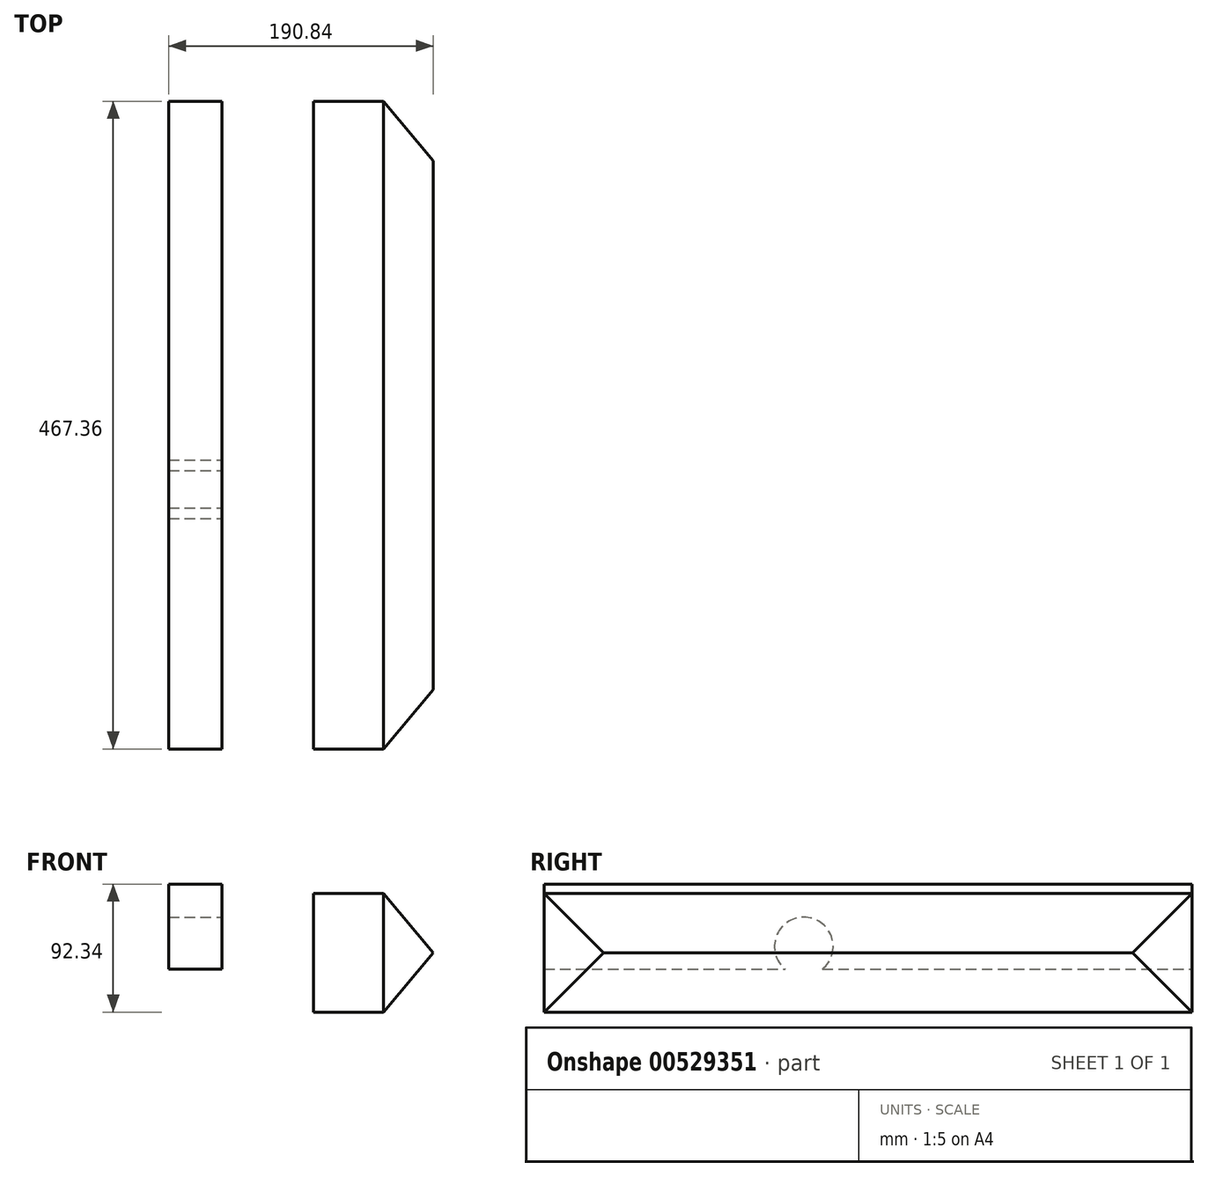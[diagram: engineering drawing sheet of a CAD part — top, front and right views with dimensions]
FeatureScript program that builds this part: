
annotation { "Feature Type Name" : "Feature", "Feature Type Description" : "" }
export const myFeature = defineFeature(function(context is Context, id is Id, definition is map)
    precondition{}
    {
        {
            var Q0;
            Q0=qCreatedBy(makeId("Front.planeOp"),FACE);
            var sketch = newSketch(context, id + "F0", { "sketchPlane" : qUnion([Q0])});
            skLineSegment(sketch, "E0.bottom", {"start": v(-55.25, 54.7) * mm, "end": v(-16.83, 54.7) * mm});
            skLineSegment(sketch, "E0.top", {"start": v(-55.25, -6.63) * mm, "end": v(-16.83, -6.63) * mm});
            skLineSegment(sketch, "E0.left", {"start": v(-55.25, 54.7) * mm, "end": v(-55.25, -6.63) * mm});
            skLineSegment(sketch, "E0.right", {"start": v(-16.83, 54.7) * mm, "end": v(-16.83, -6.63) * mm});
            skLineSegment(sketch, "E1.bottom", {"start": v(49.3, 48.02) * mm, "end": v(99.65, 48.02) * mm});
            skLineSegment(sketch, "E1.top", {"start": v(49.3, -37.65) * mm, "end": v(99.65, -37.65) * mm});
            skLineSegment(sketch, "E1.left", {"start": v(49.3, 48.02) * mm, "end": v(49.3, -37.65) * mm});
            skLineSegment(sketch, "E1.right", {"start": v(99.65, 48.02) * mm, "end": v(99.65, -37.65) * mm});
            skSolve(sketch);
        }
        {
            var Q0;
            Q0 = qSketchRegion(id + "F0", true);
            extrude(context, id + "F1", {"entities" : qUnion([Q0]), "depth" : 467.36 * mm, "offsetDistance" : 25.4 * mm});
        }
        {
            var Q0;
            Q0=makeQuery(id+"F1.opExtrude","SWEPT_FACE",FACE,{"disambiguationData":[OSD([sQuery(id+"F0.wireOp",EDGE,"E1.right")])]});
            var sketch = newSketch(context, id + "F2", { "sketchPlane" : qUnion([Q0])});
            skPoint(sketch, "E2", {"position": v(-280.03, 9.7) * mm});
            skSolve(sketch);
        }
        {
            var Q0;
            Q0=sQuery(id+"F2.wireOp",VERTEX,"E2");
            var Q1;
            Q1=makeQuery(id+"F1.opExtrude","SWEPT_BODY",BODY,{"disambiguationData":[OSD([sQuery(id+"F0.wireOp",EDGE,"E0.bottom"),sQuery(id+"F0.wireOp",EDGE,"E0.top"),sQuery(id+"F0.wireOp",EDGE,"E0.left"),sQuery(id+"F0.wireOp",EDGE,"E0.right")])]});
            hole(context, id + "F3", {"style" : HoleStyle.SIMPLE, "endStyle" : HoleEndStyle.THROUGH, "holeDiameter" : 42.32 * mm, "isTappedThrough" : true, "tappedDepth" : 12.7 * mm, "tapClearance" : 3, "startFromSketch" : true, "locations" : qUnion([Q0]), "scope" : qUnion([Q1])});
        }
        {
            var Q0;
            Q0=makeQuery(id+"F1.opExtrude","SWEPT_FACE",FACE,{"disambiguationData":[OSD([sQuery(id+"F0.wireOp",EDGE,"E1.right")])]});
            extrude(context, id + "F4", {"entities" : qUnion([Q0]), "operationType" : NewBodyOperationType.ADD, "depth" : 294.64 * mm, "offsetDistance" : 25.4 * mm, "hasDraft" : true, "draftAngle" : 50 * degree, "draftPullDirection" : true, "hasSecondDirection" : true, "secondDirectionOppositeDirection" : true, "secondDirectionDepth" : 165.35 * mm, "hasSecondDirectionDraft" : true, "secondDirectionDraftAngle" : 50 * degree, "secondDirectionDraftPullDirection" : true});
        }
    });
